# Revit family: Heatrae Sadia Multipoint Eco 30L & 50L H 3kW
name_source: partatom
category: Mechanical Equipment
revit_build: Autodesk Revit 2017 (Build: 20160225_1515(x64)
units: mm (PartAtom-declared; Revit-internal decimal feet)

## family parameters
Cut with Voids When Loaded = No
Host = Face
OmniClass Number = 23.65.35.11.11
OmniClass Title = Storage Water Heaters
Part Type = Normal
Room Calculation Point = No
Round Connector Dimension = Use Diameter
Shared = No

## types (2) — shared parameters
Arrangement = KIWA, NEMKO, CE
AssetType = Fixed
CasingFinish = White Enameled Steel
Category = Pr_60_60_96_28:Electric storage water heaters
ClearanceZoneMaterial = NBS_ClearanceZone
ColdWaterInletDiameter = 22 mm  [stored 0.0721785 ft]
Color = White
Controls = Smart Thermostatic Control
Default Elevation = 1200 mm
Description = Unvented water heater
DurationUnit = year
Finish = White Enameled Steel
FlowRate = 20 l/min
HasSwitch = Yes
HasTemperatureAndPressureReliefValve = Yes
Height = 371 mm  [stored 1.21719 ft]
HotWaterOutletDiameter = 22 mm  [stored 0.0721785 ft]
IfcExportAs = IfcBoilerType
IfcExportType = USERDEFINED
IsWaterStorageHeater = Yes
LHSClearanceZone = 300 mm
ManufacturerName = Heatrae Sadia Heating
ManufacturerURL = www.heatraesadia.com
Material = NBS_Concept
NBSCertification = www.nationalbimlibrary.com/cert/wpqzk5cm
NBSDescription = Storage water heaters, electric
NominalEfficiency = 40
NominalWidth = 371 mm  [stored 1.21719 ft]
OffsetFromWall = 12 mm  [stored 0.0393701 ft]
OutletTemperatureRange = 10°C to 70°C
PressureRating = 600 kPa
PressureReliefValvePosition = 136 mm
ProductInformation = https://www.heatraesadia.com
Rating = 3 kW
SupportPosition = 94 mm  [stored 0.308399 ft]
TemperatureAndPressureReliefValveConnectionDiameter = 15 mm  [stored 0.0492126 ft]
ThirdPartyCertification = EN55014-1:2017, EN55014-2:2015, EN60335-1:2012;A11:2014;A13:2017, EN60335-2-21:2003+A1:2005+A2:2008, EN61000-3-2:2014 & EN61000-3-3:2013, EN62233:2008, EN50440, EN60379
Uniclass2015Code = Pr_60_60_96_28
Uniclass2015Title = Electric storage water heaters
Uniclass2015Version = Products v1.7
Version = 2
WarrantyDurationParts = 2
WarrantyDurationUnit = year
WaterConnectionPosition = 83 mm  [stored 0.27231 ft]
zero-valued in all types: AboveClearanceZone, BelowClearanceZone, FrontClearanceZone, HeatOutput, NominalPartLoadRatio, RHSClearanceZone

## per-type parameters (varying)
| type | BIMObjectName | Capacity | Length | ModelReference | Name | NominalEnergyConsumption | NominalHeight | NominalLength | Shape | WaterStorageCapacity | Weight | Width |
| Multipoint Eco 30L H 3kW | Heatrae Sadia Multipoint Eco 30H | 30 L | 626 mm | Multipoint 30L H 3kW | StorageWaterHeaters,Electric_Multipoint30LH3kW_HeatraeSadiaHeating | 3 mm  [stored 0.00984252 ft] | 712 mm  [stored 2.33596 ft] | 367 mm  [stored 1.20407 ft] | 355 x 371 x 626 mm | 30 L | 14 kg | 355 mm |
| Multipoint Eco 50L H 3kW | Heatrae Sadia Multipoint Eco 50H | 50 L | 911 mm  [stored 2.98885 ft] | Multipoint 50L H 3kW | StorageWaterHeaters, Multipoint Eco 50L H 3kW | 7 mm  [stored 0.0229659 ft] | 997 mm | 355 mm | 355 x 371 x 911 mm | 50 L | 21 kg | 343 mm |

note: [stored X ft] marks values corroborated as IEEE doubles in the binary element streams (Revit-internal decimal feet)

## geometry (parser evidence)
native form markers: Sweep x4
no freeform markers — native parametric forms only
